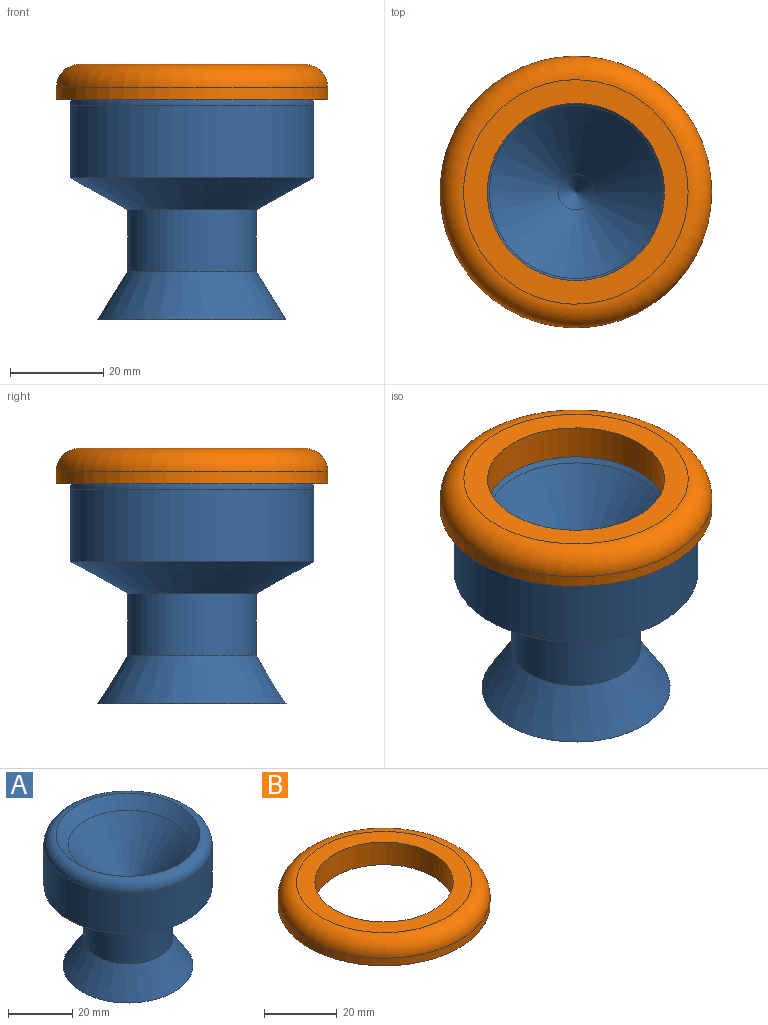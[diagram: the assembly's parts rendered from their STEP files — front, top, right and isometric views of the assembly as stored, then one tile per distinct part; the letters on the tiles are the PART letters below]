
ASSEMBLY  parts=2 mates=1
PART A: 10 faces, bbox 56.7x56.7x49.9 mm
  f0: cone r=13.83mm half-angle=31.6deg, axis (0,0,-1), area 1305.3mm2, adj f1,f9
  f1: cylinder r=13.83mm len=27.67mm, axis (0,0,1), area 1153.7mm2, adj f0,f2
  f2: cone r=26.21mm half-angle=61deg, axis (0,0,1), area 1779.9mm2, adj f1,f3
  f3: cylinder r=26.21mm len=52.42mm, axis (0,0,1), area 2556.6mm2, adj f2,f4
  f4: torus R=22.4mm, axis (0,0,1), area 933.5mm2, adj f3,f5
  f5: cone r=22.4mm half-angle=45deg, axis (0,0,1), area 693.9mm2, adj f4,f6
  f6: cone r=18.59mm half-angle=41.4deg, axis (0,0,1), area 1573.7mm2, adj f5,f7
  f7: cylinder r=3.82mm len=14.23mm, axis (0,0,1), area 342mm2, adj f6,f8
  f8: cone r=3.82mm half-angle=41.4deg, axis (0,0,1), area 69.5mm2, adj f7
  f9: plane 40.44x40.44mm, normal (0,0,-1), area 1284.6mm2, adj f0
PART B: 5 faces, bbox 63.2x63.2x7.6 mm
  f0: cylinder r=19.05mm len=38.1mm, axis (0,0,-1), area 912.1mm2, adj f2,f3
  f1: cylinder r=29.21mm len=58.42mm, axis (0,0,-1), area 466.2mm2, adj f3,f4
  f2: plane 48.26x48.26mm, normal (0,0,1), area 689.1mm2, adj f0,f4
  f3: plane 58.42x58.42mm, normal (0,0,-1), area 1540.4mm2, adj f0,f1
  f4: torus R=24.13mm, axis (0,0,1), area 1372mm2, adj f1,f2
PLACE A t=(-6.15,-7.51,3.91)mm
PLACE B t=(-6.15,-7.51,12.4)mm
MATE revolute B.f0 <-> A.f0  axis (0,0,1) through (-6.15,-7.51,14.94)mm
